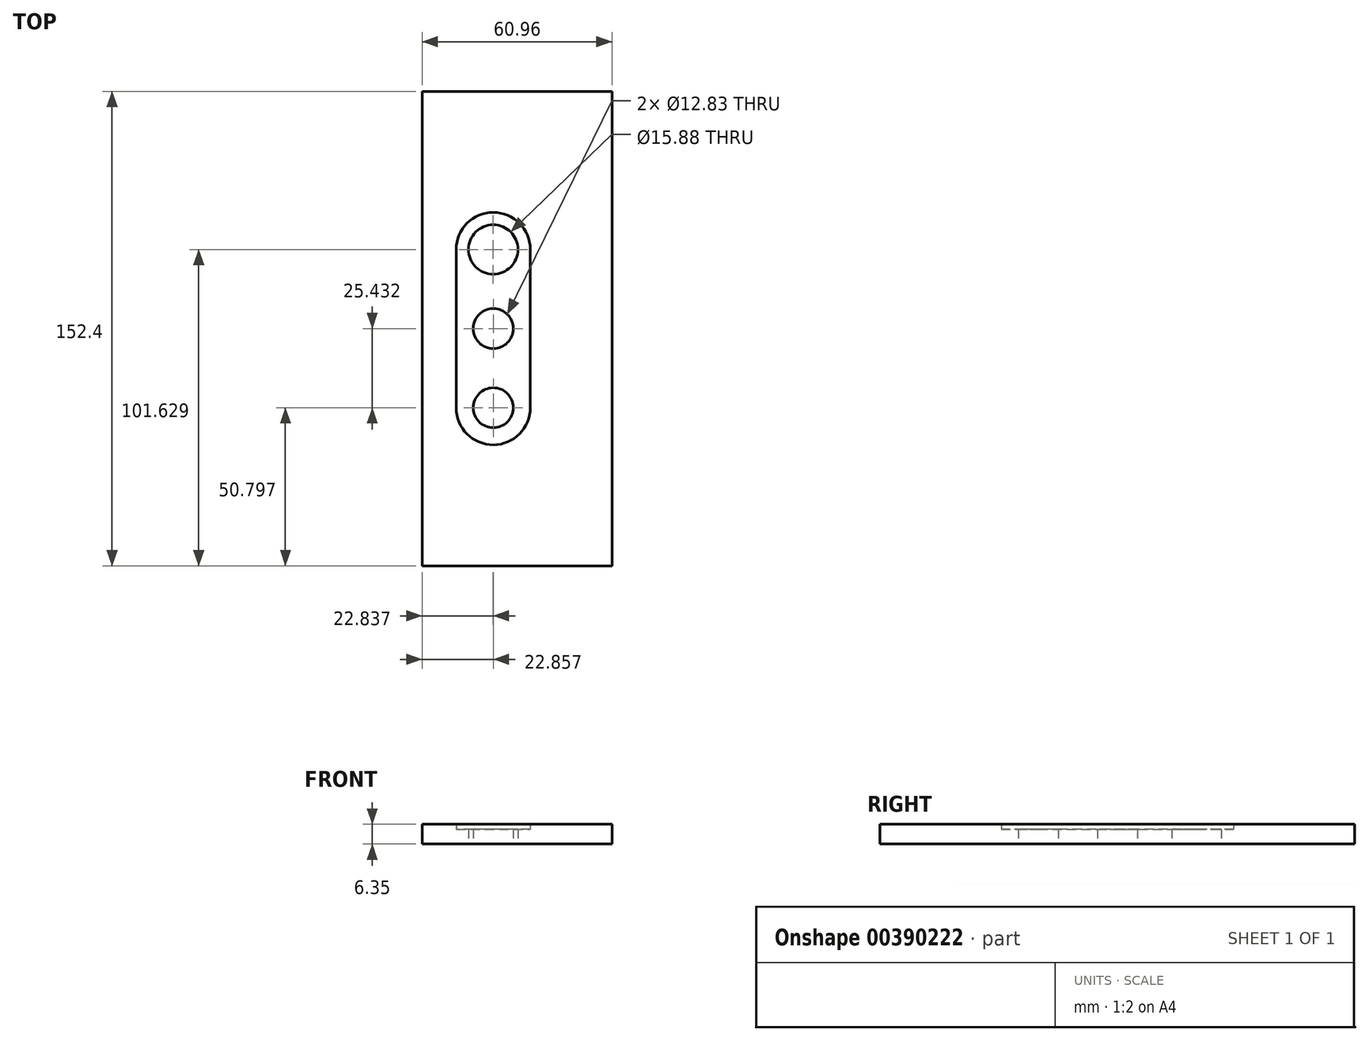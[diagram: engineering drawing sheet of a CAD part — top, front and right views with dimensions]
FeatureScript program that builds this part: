
annotation { "Feature Type Name" : "Feature", "Feature Type Description" : "" }
export const myFeature = defineFeature(function(context is Context, id is Id, definition is map)
    precondition{}
    {
        {
            var Q0;
            Q0=qCreatedBy(makeId("Top.planeOp"),FACE);
            var sketch = newSketch(context, id + "F0", { "sketchPlane" : qUnion([Q0]), "disableImprinting" : false});
            skLineSegment(sketch, "E0.bottom", {"start": v(-22.86, 76.2) * mm, "end": v(-22.86, -76.2) * mm});
            skLineSegment(sketch, "E0.top", {"start": v(38.1, 76.2) * mm, "end": v(38.1, -76.2) * mm});
            skLineSegment(sketch, "E0.left", {"start": v(38.1, 76.2) * mm, "end": v(-22.86, 76.2) * mm});
            skLineSegment(sketch, "E0.right", {"start": v(38.1, -76.2) * mm, "end": v(-22.86, -76.2) * mm});
            skCircle(sketch, "E1.1.0.0", {"center": v(0, 0.04) * mm, "radius": 6.41 * mm});
            skCircle(sketch, "E2.1.0.0", {"center": v(0, -25.4) * mm, "radius": 6.41 * mm});
            skCircle(sketch, "E3.1.0.0", {"center": v(-0.02, 25.44) * mm, "radius": 7.94 * mm});
            skPoint(sketch, "E4.orphan", {"position": v(0, 0) * mm});
            skCircle(sketch, "E5", {"center": v(0, -25.4) * mm, "radius": 11.9 * mm});
            skCircle(sketch, "E6", {"center": v(-0.02, 25.44) * mm, "radius": 11.9 * mm});
            skLineSegment(sketch, "E7", {"start": v(-11.9, -25.4) * mm, "end": v(-11.93, 25.43) * mm});
            skLineSegment(sketch, "E8", {"start": v(11.88, 25.44) * mm, "end": v(11.9, -25.39) * mm});
            skSolve(sketch);
        }
        {
            var Q0;
            Q0=makeQuery(id+"F0.imprint","IMPRINT",FACE,{"disambiguationData":[TD([[makeQuery(id+"F0.imprint","IMPRINT",EDGE,{"derivedFrom":sQuery(id+"F0.wireOp",EDGE,"E1.1.0.0")}),-1.0]])]});
            var Q1;
            Q1=makeQuery(id+"F0.imprint","IMPRINT",FACE,{"disambiguationData":[TD([[makeQuery(id+"F0.imprint","IMPRINT",EDGE,{"derivedFrom":sQuery(id+"F0.wireOp",EDGE,"E3.1.0.0")}),-1.0]])]});
            var Q2;
            Q2=makeQuery(id+"F0.imprint","IMPRINT",FACE,{"disambiguationData":[TD([[makeQuery(id+"F0.imprint","IMPRINT",EDGE,{"derivedFrom":sQuery(id+"F0.wireOp",EDGE,"E2.1.0.0")}),-1.0]])]});
            extrude(context, id + "F1", {"entities" : qUnion([Q0, Q1, Q2]), "depth" : 4.76 * mm});
        }
        {
            var Q0;
            Q0=makeQuery(id+"F0.imprint","IMPRINT",FACE,{"disambiguationData":[TD([[makeQuery(id+"F0.imprint","IMPRINT",EDGE,{"derivedFrom":sQuery(id+"F0.wireOp",EDGE,"E0.bottom")}),1.0]])]});
            extrude(context, id + "F2", {"entities" : qUnion([Q0]), "operationType" : NewBodyOperationType.ADD, "depth" : 6.35 * mm});
        }
        {
            var Q0;
            Q0=makeQuery(id+"F1.opExtrude","SWEPT_BODY",BODY,{"disambiguationData":[OSD([sQuery(id+"F0.wireOp",EDGE,"E1.1.0.0"),sQuery(id+"F0.wireOp",EDGE,"E2.1.0.0"),sQuery(id+"F0.wireOp",EDGE,"E3.1.0.0"),sQuery(id+"F0.wireOp",EDGE,"E5"),sQuery(id+"F0.wireOp",EDGE,"E6"),sQuery(id+"F0.wireOp",EDGE,"E7"),sQuery(id+"F0.wireOp",EDGE,"E8")])]});
            transform(context, id + "F3", {"entities" : qUnion([Q0]), "transformType" : TransformType.TRANSLATION_3D, "dx" : 0 * mm, "dy" : 0 * mm, "dz" : -6.35 * mm, "makeCopy" : false});
        }
    });
